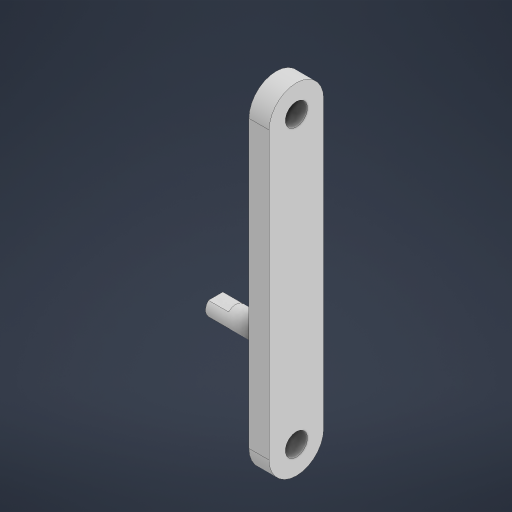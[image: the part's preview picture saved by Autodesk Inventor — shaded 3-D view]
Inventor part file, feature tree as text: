
AUTODESK INVENTOR PART (.ipt)
format: ipt  version: 2024 (Build 280153000, 153)  size: 443,392 bytes
history: native  units: mm
features: extrude x3, sketch x1
ambient origin geometry x8: Origin, YZ Plane, XZ Plane, XY Plane, X Axis, Y Axis, Z Axis, Center Point
bodies: Body1 (feature_tree)
feature tree (4):
  sketch  "스케치4"
  extrude  "돌출6"  Depth=5.5mm
  extrude  "돌출7"  Depth=13.5mm
  extrude  "돌출8"  Depth=70.8mm
